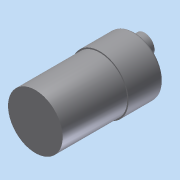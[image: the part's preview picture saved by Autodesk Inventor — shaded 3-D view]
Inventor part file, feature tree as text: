
AUTODESK INVENTOR PART (.ipt)
format: ipt  version: 2012 (Build 160160000, 160)  size: 109,056 bytes
history: native  units: in
note: dims shown in document units (in); Inventor stores cm internally (conversion verified against a paired STEP export)
features: sketch x4, extrude x3, fillet x1, hole x1
ambient origin geometry x8: Origin, YZ Plane, XZ Plane, XY Plane, X Axis, Y Axis, Z Axis, Center Point
bodies: Solid1 (feature_tree)
feature tree (9):
  extrude  "Extrusion1"  Depth=0.875in TaperAngle=0.0deg
  extrude  "Extrusion2"  Depth=1.625in TaperAngle=0.0deg
  fillet  "Fillet1"  Radius=0.0625in
  extrude  "Extrusion3"  Depth=0.3125in
  hole  "Hole1"  [1 undecoded]
  sketch  "Sketch1"  dims[d0=1.4375in d1=0.875in d2=0.0in]
  sketch  "Sketch2"  dims[d3=1.375in d4=1.625in d5=0.0in d6=0.0625in]
  sketch  "Sketch3"  dims[d7=0.5in d8=0.3125in]
  sketch  "Sketch4"  dims[d9=0.25in d10=0.0in d11=0.25in d12=0.25in d13=0.75in d14=0.375in d15=0.25in d16=0.5635in d17=0.25in d18=0.0in d19=1.0in d20=1.0in]
note: 1 required parameter value undecoded (feature->parameter linkage not recoverable at this tier; creation-order binding heuristic only, values carry confidence <= 0.55)
